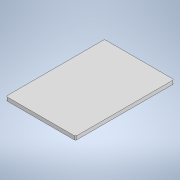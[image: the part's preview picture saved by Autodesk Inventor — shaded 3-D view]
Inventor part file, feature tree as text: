
AUTODESK INVENTOR PART (.ipt)
format: ipt  version: 2021 (Build 250183000, 183)  size: 115,200 bytes
history: native  units: mm
features: extrude x2, sketch x2, other x1, fillet x1
ambient origin geometry x8: Origin, YZ Plane, XZ Plane, XY Plane, X Axis, Y Axis, Z Axis, Center Point
bodies: Body1 (feature_tree)
feature tree (6):
  other  "Bryła1"
  extrude  "Wyciągnięcie proste1"  Depth=192.0mm
  fillet  "Zaokrąglenie1"  Radius=272.0mm
  extrude  "Wyciągnięcie proste3"  Depth=10.0mm TaperAngle=0.0deg
  sketch  "Szkic2"
  sketch  "Szkic4"
